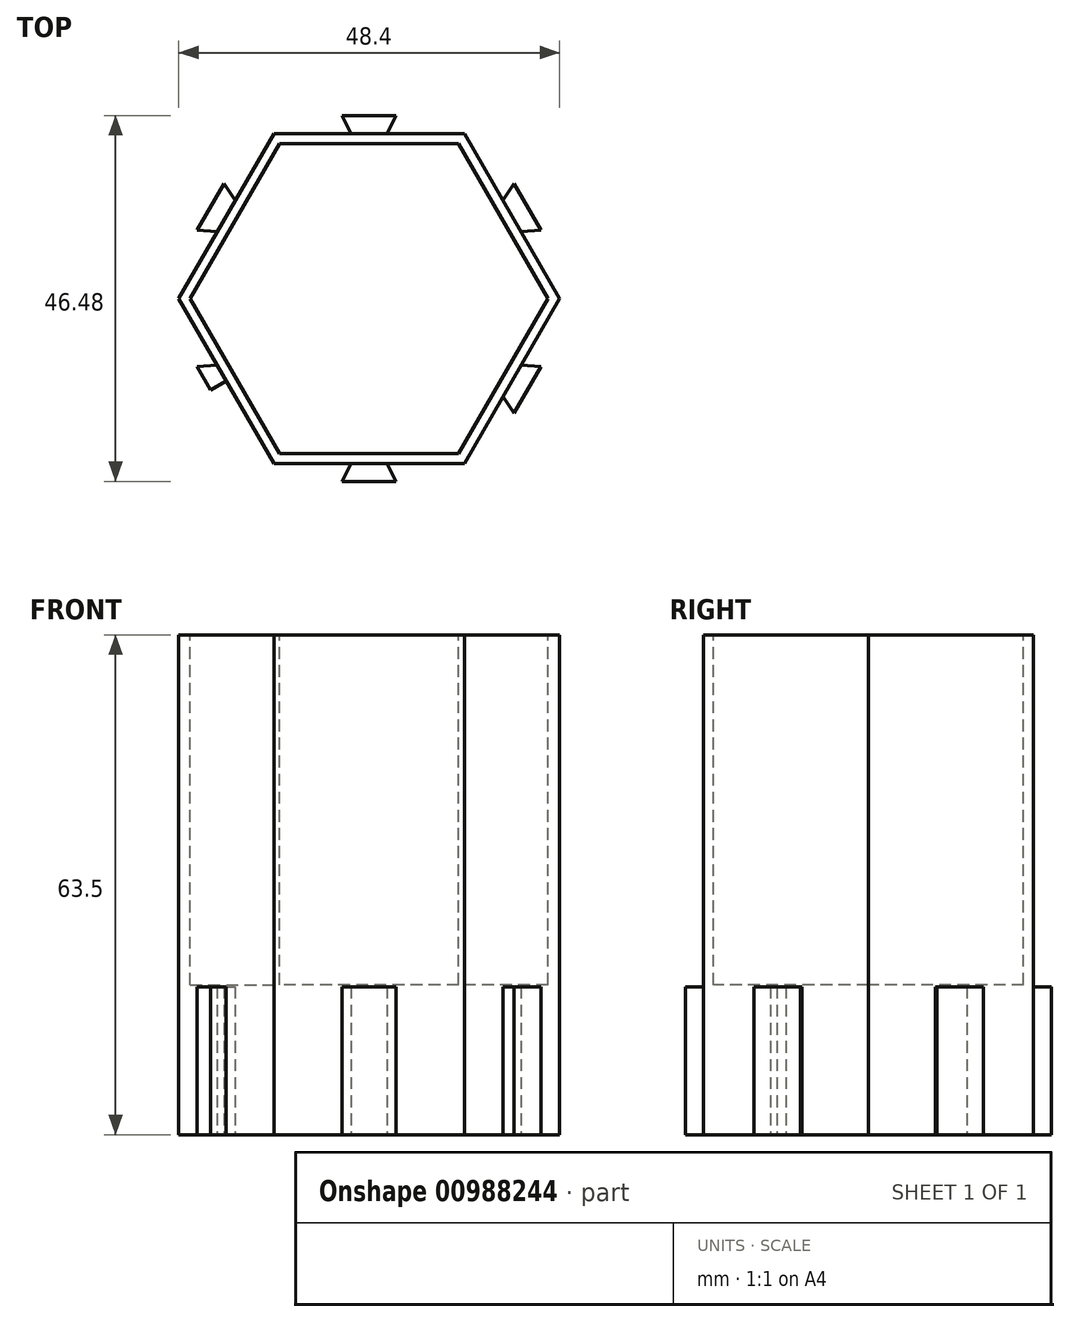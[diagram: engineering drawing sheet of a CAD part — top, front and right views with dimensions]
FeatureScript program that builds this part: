
annotation { "Feature Type Name" : "Feature", "Feature Type Description" : "" }
export const myFeature = defineFeature(function(context is Context, id is Id, definition is map)
    precondition{}
    {
        {
            var Q0;
            Q0=qCreatedBy(makeId("Top.planeOp"),FACE);
            var sketch = newSketch(context, id + "F0", { "sketchPlane" : qUnion([Q0])});
            skCircle(sketch, "E0.cCircle", {"center": v(0, 0) * mm, "radius": 20.96 * mm, "construction": true});
            skLineSegment(sketch, "E0.0", {"start": v(12.1, -20.96) * mm, "end": v(-12.1, -20.96) * mm});
            skLineSegment(sketch, "E0.1", {"start": v(-12.1, -20.96) * mm, "end": v(-24.2, 0) * mm});
            skLineSegment(sketch, "E0.2", {"start": v(-24.2, 0) * mm, "end": v(-12.1, 20.96) * mm});
            skLineSegment(sketch, "E0.3", {"start": v(-12.1, 20.95) * mm, "end": v(12.1, 20.96) * mm});
            skLineSegment(sketch, "E0.4", {"start": v(12.1, 20.96) * mm, "end": v(24.2, 0) * mm});
            skLineSegment(sketch, "E0.5", {"start": v(24.2, 0) * mm, "end": v(12.1, -20.95) * mm});
            skPoint(sketch, "E0.0.midPoint", {"position": v(0, -20.96) * mm});
            skSolve(sketch);
        }
        {
            var Q0;
            Q0=makeQuery(id+"F0.imprint","IMPRINT",FACE,{"disambiguationData":[TD([[makeQuery(id+"F0.imprint","IMPRINT",EDGE,{"derivedFrom":sQuery(id+"F0.wireOp",EDGE,"E0.0")}),-1.0]])]});
            extrude(context, id + "F1", {"entities" : qUnion([Q0]), "depth" : 63.5 * mm, "offsetDistance" : 25.4 * mm});
        }
        {
            var Q0;
            Q0=makeQuery(id+"F1.opExtrude","CAP_FACE",FACE,{"disambiguationData":[OSD([sQuery(id+"F0.wireOp",EDGE,"E0.0"),sQuery(id+"F0.wireOp",EDGE,"E0.1"),sQuery(id+"F0.wireOp",EDGE,"E0.2"),sQuery(id+"F0.wireOp",EDGE,"E0.3"),sQuery(id+"F0.wireOp",EDGE,"E0.4"),sQuery(id+"F0.wireOp",EDGE,"E0.5")])],"isStart":false});
            var sketch = newSketch(context, id + "F2", { "sketchPlane" : qUnion([Q0])});
            skCircle(sketch, "E1.cCircle", {"center": v(0, 0) * mm, "radius": 19.69 * mm, "construction": true});
            skLineSegment(sketch, "E1.0", {"start": v(11.37, -19.69) * mm, "end": v(-11.37, -19.69) * mm});
            skLineSegment(sketch, "E1.1", {"start": v(-11.37, -19.69) * mm, "end": v(-22.73, 0) * mm});
            skLineSegment(sketch, "E1.2", {"start": v(-22.73, 0) * mm, "end": v(-11.37, 19.69) * mm});
            skLineSegment(sketch, "E1.3", {"start": v(-11.37, 19.68) * mm, "end": v(11.37, 19.69) * mm});
            skLineSegment(sketch, "E1.4", {"start": v(11.37, 19.69) * mm, "end": v(22.73, 0) * mm});
            skLineSegment(sketch, "E1.5", {"start": v(22.73, 0) * mm, "end": v(11.37, -19.69) * mm});
            skPoint(sketch, "E1.0.midPoint", {"position": v(0, -19.69) * mm});
            skSolve(sketch);
        }
        {
            var Q0;
            Q0=makeQuery(id+"F2.imprint","IMPRINT",FACE,{"disambiguationData":[TD([[makeQuery(id+"F2.imprint","IMPRINT",EDGE,{"derivedFrom":sQuery(id+"F2.wireOp",EDGE,"E1.0")}),-1.0]])]});
            extrude(context, id + "F3", {"entities" : qUnion([Q0]), "operationType" : NewBodyOperationType.REMOVE, "oppositeDirection" : true, "depth" : 44.45 * mm, "offsetDistance" : 25.4 * mm});
        }
        {
            var Q0;
            Q0=makeQuery(id+"F1.opExtrude","CAP_FACE",FACE,{"disambiguationData":[OSD([sQuery(id+"F0.wireOp",EDGE,"E0.0"),sQuery(id+"F0.wireOp",EDGE,"E0.1"),sQuery(id+"F0.wireOp",EDGE,"E0.2"),sQuery(id+"F0.wireOp",EDGE,"E0.3"),sQuery(id+"F0.wireOp",EDGE,"E0.4"),sQuery(id+"F0.wireOp",EDGE,"E0.5")])],"isStart":true});
            var sketch = newSketch(context, id + "F4", { "sketchPlane" : qUnion([Q0])});
            skLineSegment(sketch, "E2", {"start": v(-18.15, -10.48) * mm, "end": v(18.15, 10.48) * mm});
            skPoint(sketch, "E2.startSnap0", {"position": v(-18.15, -10.48) * mm});
            skLineSegment(sketch, "E3", {"start": v(-18.15, 10.48) * mm, "end": v(18.15, -10.48) * mm});
            skLineSegment(sketch, "E4", {"start": v(0, 20.96) * mm, "end": v(0, -20.96) * mm});
            skLineSegment(sketch, "E5", {"start": v(-12.1, 20.95) * mm, "end": v(12.1, -20.96) * mm});
            skLineSegment(sketch, "E6", {"start": v(-24.2, 0) * mm, "end": v(24.2, 0) * mm});
            skLineSegment(sketch, "E7", {"start": v(12.1, 20.95) * mm, "end": v(-12.1, -20.95) * mm});
            skLineSegment(sketch, "E8", {"start": v(0, -20.96) * mm, "end": v(0, -23.24) * mm});
            skLineSegment(sketch, "E9", {"start": v(0, -23.24) * mm, "end": v(3.43, -23.24) * mm});
            skLineSegment(sketch, "E10", {"start": v(0, -20.96) * mm, "end": v(2.29, -20.96) * mm});
            skLineSegment(sketch, "E11", {"start": v(2.29, -20.96) * mm, "end": v(3.43, -23.24) * mm});
            skLineSegment(sketch, "E12.MirrorCS", {"start": v(0, -23.24) * mm, "end": v(-3.43, -23.24) * mm});
            skLineSegment(sketch, "E13.MirrorCS", {"start": v(0, -20.96) * mm, "end": v(-2.29, -20.96) * mm});
            skLineSegment(sketch, "E14.MirrorCS", {"start": v(-2.29, -20.96) * mm, "end": v(-3.43, -23.24) * mm});
            skLineSegment(sketch, "E15.MirrorCS", {"start": v(-2.29, 20.96) * mm, "end": v(-3.43, 23.24) * mm});
            skLineSegment(sketch, "E16.MirrorCS", {"start": v(0, 20.95) * mm, "end": v(-2.29, 20.95) * mm});
            skLineSegment(sketch, "E17.MirrorCS", {"start": v(0, 20.95) * mm, "end": v(2.29, 20.95) * mm});
            skLineSegment(sketch, "E18.MirrorCS", {"start": v(0, 23.24) * mm, "end": v(-3.43, 23.24) * mm});
            skLineSegment(sketch, "E19.MirrorCS", {"start": v(0, 23.24) * mm, "end": v(3.43, 23.24) * mm});
            skLineSegment(sketch, "E20.MirrorCS", {"start": v(2.29, 20.96) * mm, "end": v(3.43, 23.24) * mm});
            skLineSegment(sketch, "E21", {"start": v(-18.15, -10.48) * mm, "end": v(-19.3, -8.5) * mm});
            skLineSegment(sketch, "E22", {"start": v(-18.15, -10.48) * mm, "end": v(-20.13, -11.62) * mm});
            skLineSegment(sketch, "E23", {"start": v(-20.13, -11.62) * mm, "end": v(-21.84, -8.65) * mm});
            skLineSegment(sketch, "E24", {"start": v(-21.84, -8.65) * mm, "end": v(-19.3, -8.5) * mm});
            skLineSegment(sketch, "E25.MirrorCS", {"start": v(-20.13, -11.62) * mm, "end": v(-18.41, -14.6) * mm});
            skLineSegment(sketch, "E26.MirrorCS", {"start": v(-18.41, -14.6) * mm, "end": v(-17, -12.46) * mm});
            skLineSegment(sketch, "E27.MirrorCS", {"start": v(-18.15, -10.48) * mm, "end": v(-17, -12.46) * mm});
            skLineSegment(sketch, "E28.MirrorCS", {"start": v(20.13, 11.62) * mm, "end": v(21.84, 8.65) * mm});
            skLineSegment(sketch, "E29.MirrorCS", {"start": v(21.84, 8.65) * mm, "end": v(19.3, 8.5) * mm});
            skLineSegment(sketch, "E30.MirrorCS", {"start": v(18.15, 10.48) * mm, "end": v(19.3, 8.5) * mm});
            skLineSegment(sketch, "E31.MirrorCS", {"start": v(18.15, 10.48) * mm, "end": v(17, 12.46) * mm});
            skLineSegment(sketch, "E32.MirrorCS", {"start": v(20.13, 11.62) * mm, "end": v(18.41, 14.6) * mm});
            skLineSegment(sketch, "E33.MirrorCS", {"start": v(18.41, 14.6) * mm, "end": v(17, 12.46) * mm});
            skLineSegment(sketch, "E34", {"start": v(-18.15, 10.48) * mm, "end": v(-19.3, 8.5) * mm});
            skLineSegment(sketch, "E35", {"start": v(-18.15, 10.48) * mm, "end": v(-20.13, 11.62) * mm});
            skLineSegment(sketch, "E36", {"start": v(-20.13, 11.62) * mm, "end": v(-21.84, 8.65) * mm});
            skLineSegment(sketch, "E37", {"start": v(-21.84, 8.65) * mm, "end": v(-19.3, 8.5) * mm});
            skLineSegment(sketch, "E38.MirrorCS", {"start": v(-18.41, 14.6) * mm, "end": v(-17, 12.46) * mm});
            skLineSegment(sketch, "E39.MirrorCS", {"start": v(-20.13, 11.62) * mm, "end": v(-18.41, 14.6) * mm});
            skLineSegment(sketch, "E40.MirrorCS", {"start": v(-18.15, 10.48) * mm, "end": v(-17, 12.46) * mm});
            skLineSegment(sketch, "E41.MirrorCS", {"start": v(20.13, -11.62) * mm, "end": v(18.41, -14.6) * mm});
            skLineSegment(sketch, "E42.MirrorCS", {"start": v(18.41, -14.6) * mm, "end": v(17, -12.46) * mm});
            skLineSegment(sketch, "E43.MirrorCS", {"start": v(18.15, -10.48) * mm, "end": v(17, -12.46) * mm});
            skLineSegment(sketch, "E44.MirrorCS", {"start": v(20.13, -11.62) * mm, "end": v(21.84, -8.65) * mm});
            skLineSegment(sketch, "E45.MirrorCS", {"start": v(21.84, -8.65) * mm, "end": v(19.3, -8.5) * mm});
            skLineSegment(sketch, "E46.MirrorCS", {"start": v(18.15, -10.48) * mm, "end": v(19.3, -8.5) * mm});
            skSolve(sketch);
        }
        {
            var Q0;
            Q0=makeQuery(id+"F4.imprint","IMPRINT",FACE,{"disambiguationData":[TD([[makeQuery(id+"F4.imprint","IMPRINT",EDGE,{"derivedFrom":sQuery(id+"F4.wireOp",EDGE,"E15.MirrorCS")}),-1.0]])]});
            var Q1;
            Q1=makeQuery(id+"F4.imprint","IMPRINT",FACE,{"disambiguationData":[TD([[makeQuery(id+"F4.imprint","IMPRINT",EDGE,{"derivedFrom":sQuery(id+"F4.wireOp",EDGE,"E35")}),-1.0]])]});
            var Q2;
            Q2=makeQuery(id+"F4.imprint","IMPRINT",FACE,{"disambiguationData":[TD([[makeQuery(id+"F4.imprint","IMPRINT",EDGE,{"derivedFrom":sQuery(id+"F4.wireOp",EDGE,"E34")}),-1.0]])]});
            var Q3;
            Q3=makeQuery(id+"F4.imprint","IMPRINT",FACE,{"disambiguationData":[TD([[makeQuery(id+"F4.imprint","IMPRINT",EDGE,{"derivedFrom":sQuery(id+"F4.wireOp",EDGE,"E22")}),1.0]])]});
            var Q4;
            Q4=makeQuery(id+"F4.imprint","IMPRINT",FACE,{"disambiguationData":[TD([[makeQuery(id+"F4.imprint","IMPRINT",EDGE,{"derivedFrom":sQuery(id+"F4.wireOp",EDGE,"E21")}),-1.0]])]});
            var Q5;
            Q5=makeQuery(id+"F4.imprint","IMPRINT",FACE,{"disambiguationData":[TD([[makeQuery(id+"F4.imprint","IMPRINT",EDGE,{"derivedFrom":sQuery(id+"F4.wireOp",EDGE,"E8")}),-1.0]])]});
            var Q6;
            Q6=makeQuery(id+"F4.imprint","IMPRINT",FACE,{"disambiguationData":[TD([[makeQuery(id+"F4.imprint","IMPRINT",EDGE,{"derivedFrom":sQuery(id+"F4.wireOp",EDGE,"E8")}),1.0]])]});
            var Q7;
            Q7=makeQuery(id+"F4.imprint","IMPRINT",FACE,{"disambiguationData":[TD([[makeQuery(id+"F4.imprint","IMPRINT",EDGE,{"derivedFrom":sQuery(id+"F4.wireOp",EDGE,"E41.MirrorCS")}),-1.0]])]});
            var Q8;
            Q8=makeQuery(id+"F4.imprint","IMPRINT",FACE,{"disambiguationData":[TD([[makeQuery(id+"F4.imprint","IMPRINT",EDGE,{"derivedFrom":sQuery(id+"F4.wireOp",EDGE,"E28.MirrorCS")}),-1.0]])]});
            extrude(context, id + "F5", {"entities" : qUnion([Q0, Q1, Q2, Q3, Q4, Q5, Q6, Q7, Q8]), "operationType" : NewBodyOperationType.ADD, "oppositeDirection" : true, "depth" : 18.8 * mm, "offsetDistance" : 25.4 * mm});
        }
    });
